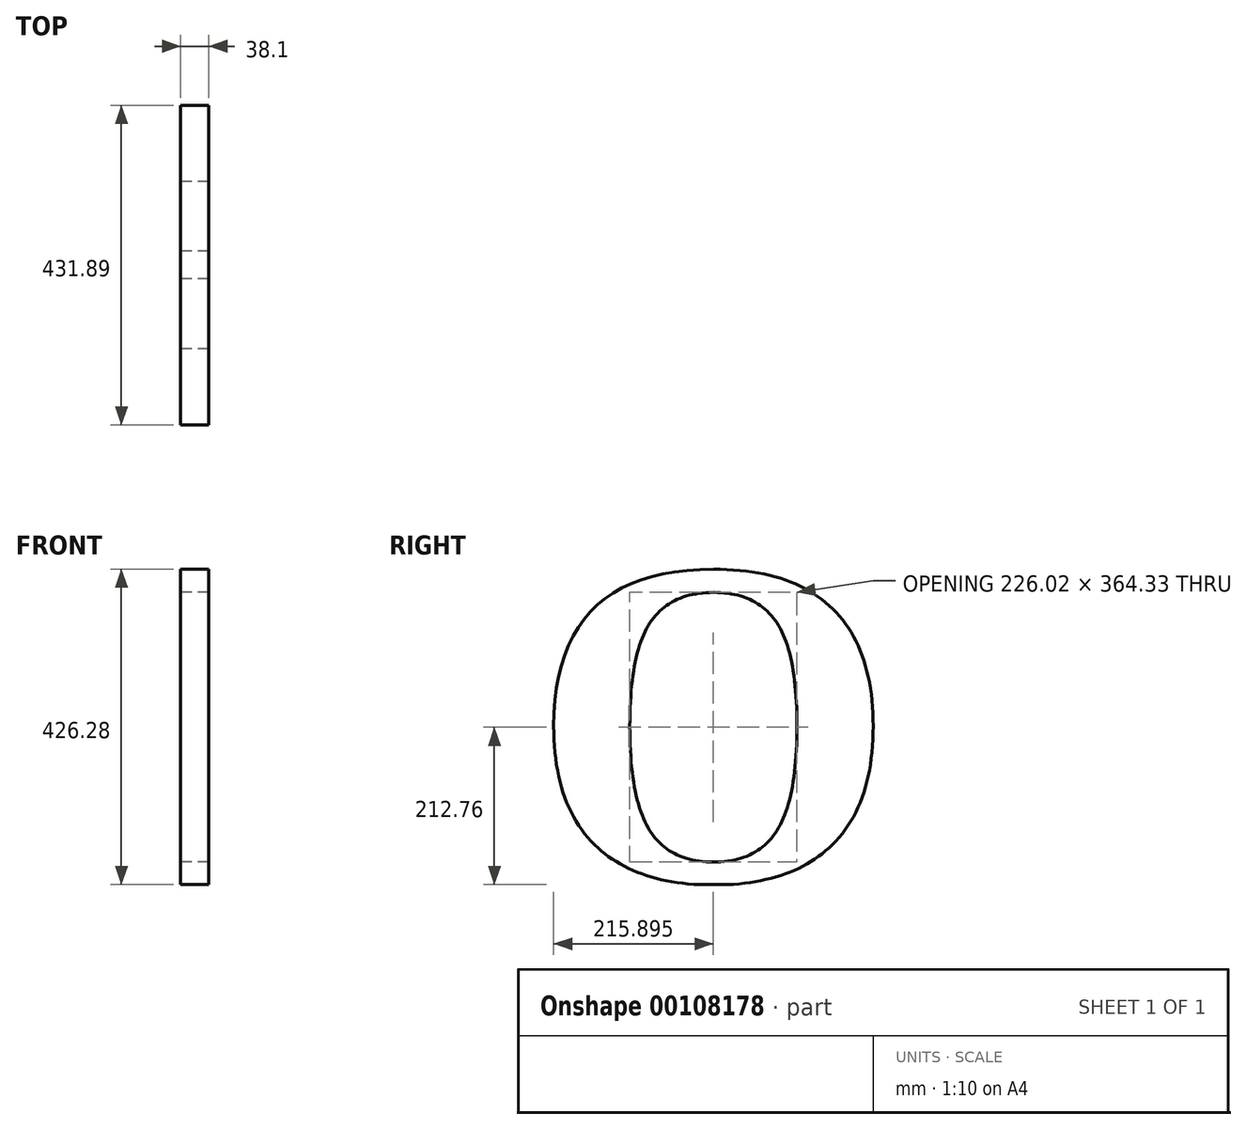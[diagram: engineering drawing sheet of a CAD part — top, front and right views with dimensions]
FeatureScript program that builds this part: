
annotation { "Feature Type Name" : "Feature", "Feature Type Description" : "" }
export const myFeature = defineFeature(function(context is Context, id is Id, definition is map)
    precondition{}
    {
        {
            var Q0;
            Q0=qCreatedBy(makeId("Right.planeOp"),FACE);
            var sketch = newSketch(context, id + "F0", { "sketchPlane" : qUnion([Q0])});
            skText(sketch, "E0", { "text": "O", "fontName": "Tinos-Bold.ttf"});
            const initialGuessF0  = {"E0": [-0.50264, 0, 1, 0, 0.4572]};
            skSetInitialGuess(sketch, initialGuessF0);
            skSolve(sketch);
        }
        {
            var Q0;
            Q0 = qSketchRegion(id + "F0", true);
            extrude(context, id + "F1", {"entities" : qUnion([Q0]), "depth" : 38.1 * mm});
        }
        {
            var Q0;
            Q0=makeQuery(id+"F1.opExtrude","CAP_FACE",FACE,{"disambiguationData":[OSD([sQuery(id+"F0.wireOp",EDGE,"E0.sketch_text.stroke-0"),sQuery(id+"F0.wireOp",EDGE,"E0.sketch_text.stroke-1"),sQuery(id+"F0.wireOp",EDGE,"E0.sketch_text.stroke-2"),sQuery(id+"F0.wireOp",EDGE,"E0.sketch_text.stroke-3"),sQuery(id+"F0.wireOp",EDGE,"E0.sketch_text.stroke-4"),sQuery(id+"F0.wireOp",EDGE,"E0.sketch_text.stroke-5"),sQuery(id+"F0.wireOp",EDGE,"E0.sketch_text.stroke-6"),sQuery(id+"F0.wireOp",EDGE,"E0.sketch_text.stroke-7"),sQuery(id+"F0.wireOp",EDGE,"E0.sketch_text.stroke-8"),sQuery(id+"F0.wireOp",EDGE,"E0.sketch_text.stroke-9"),sQuery(id+"F0.wireOp",EDGE,"E0.sketch_text.stroke-10"),sQuery(id+"F0.wireOp",EDGE,"E0.sketch_text.stroke-11"),sQuery(id+"F0.wireOp",EDGE,"E0.sketch_text.stroke-12"),sQuery(id+"F0.wireOp",EDGE,"E0.sketch_text.stroke-13"),sQuery(id+"F0.wireOp",EDGE,"E0.sketch_text.stroke-14")])],"isStart":false});
            var sketch = newSketch(context, id + "F2", { "sketchPlane" : qUnion([Q0])});
            skLineSegment(sketch, "E1", {"start": v(-255.49, -6.25) * mm, "end": v(-255.49, -4.73) * mm, "construction": true});
            skLineSegment(sketch, "E2", {"start": v(-255.49, -4.73) * mm, "end": v(-317.02, -5.8) * mm, "construction": true});
            skLineSegment(sketch, "E3.bottom", {"start": v(-317.02, -5.8) * mm, "end": v(-183.71, -5.8) * mm});
            skLineSegment(sketch, "E3.top", {"start": v(-317.02, -11.64) * mm, "end": v(-183.71, -11.64) * mm});
            skLineSegment(sketch, "E3.left", {"start": v(-317.02, -5.8) * mm, "end": v(-317.02, -11.64) * mm});
            skLineSegment(sketch, "E3.right", {"start": v(-183.71, -5.8) * mm, "end": v(-183.71, -11.64) * mm});
            skSolve(sketch);
        }
        {
            var Q0;
            Q0 = qSketchRegion(id + "F2", true);
            extrude(context, id + "F3", {"entities" : qUnion([Q0]), "operationType" : NewBodyOperationType.REMOVE, "endBound" : BoundingType.THROUGH_ALL, "oppositeDirection" : true, "depth" : 25.4 * mm});
        }
    });
